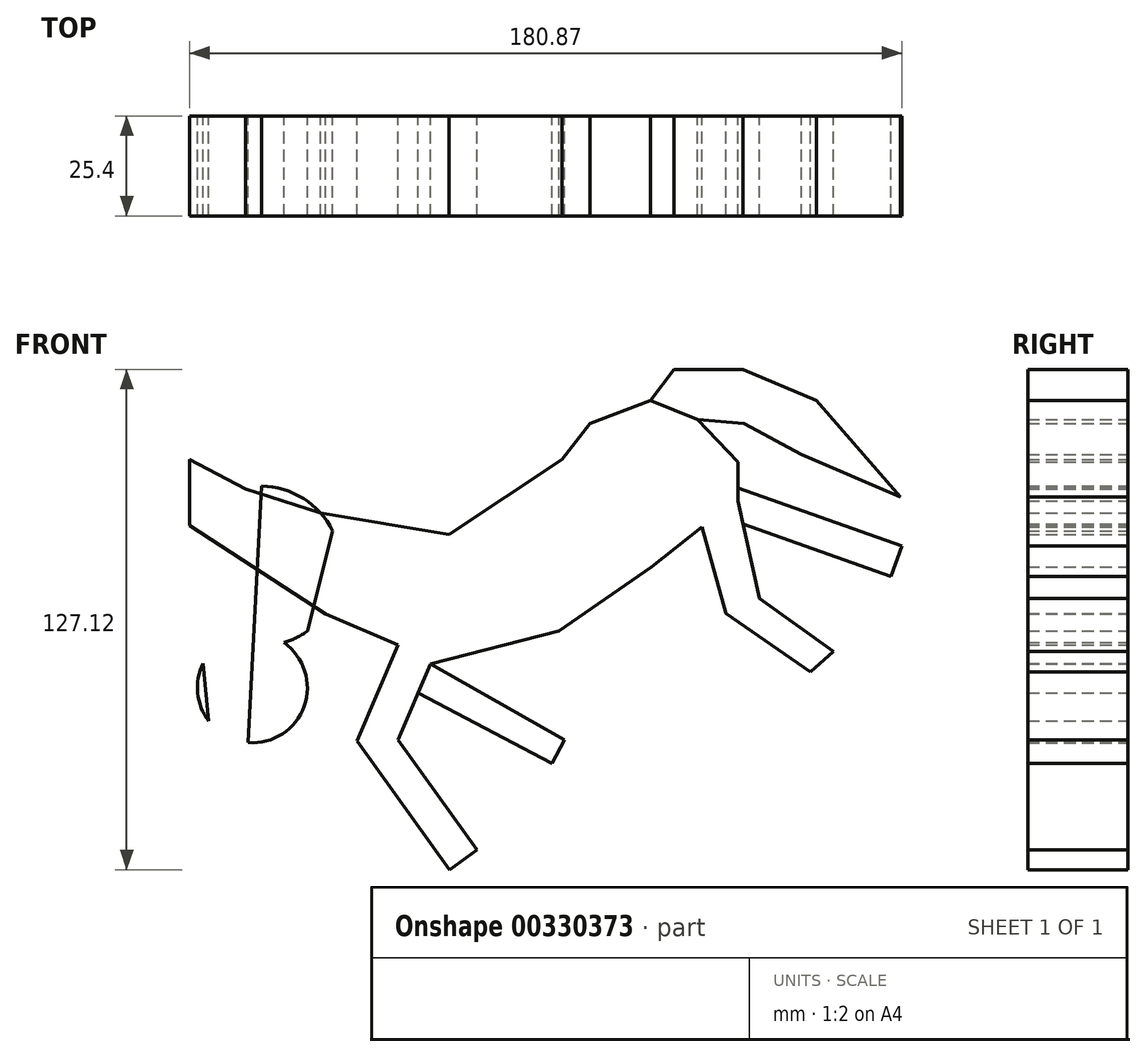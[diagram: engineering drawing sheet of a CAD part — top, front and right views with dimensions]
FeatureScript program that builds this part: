
annotation { "Feature Type Name" : "Feature", "Feature Type Description" : "" }
export const myFeature = defineFeature(function(context is Context, id is Id, definition is map)
    precondition{}
    {
        {
            var Q0;
            Q0=qCreatedBy(makeId("Front.planeOp"),FACE);
            var sketch = newSketch(context, id + "F0", { "sketchPlane" : qUnion([Q0])});
            skLineSegment(sketch, "E0.bottom", {"start": v(-85.46, 39.7) * mm, "end": v(65.16, 39.7) * mm});
            skLineSegment(sketch, "E0.top", {"start": v(-85.46, -39.7) * mm, "end": v(65.16, -39.7) * mm});
            skLineSegment(sketch, "E0.left", {"start": v(-85.46, 39.7) * mm, "end": v(-85.46, -39.7) * mm});
            skLineSegment(sketch, "E0.right", {"start": v(65.16, 39.7) * mm, "end": v(65.16, -39.7) * mm});
            skPoint(sketch, "E0.middle", {"position": v(-10.15, 0) * mm});
            skLineSegment(sketch, "E1.bottom", {"start": v(123.33, 72.62) * mm, "end": v(31.34, 72.62) * mm});
            skLineSegment(sketch, "E1.top", {"start": v(123.33, 122.22) * mm, "end": v(31.34, 122.22) * mm});
            skLineSegment(sketch, "E1.left", {"start": v(123.33, 72.62) * mm, "end": v(123.33, 122.22) * mm});
            skLineSegment(sketch, "E1.right", {"start": v(31.34, 72.62) * mm, "end": v(31.34, 122.22) * mm});
            skPoint(sketch, "E1.middle", {"position": v(77.33, 97.42) * mm});
            skLineSegment(sketch, "E2", {"start": v(68.31, 39.7) * mm, "end": v(77.33, 97.42) * mm});
            skLineSegment(sketch, "E3", {"start": v(77.33, 97.42) * mm, "end": v(-10.15, 90.2) * mm});
            skLineSegment(sketch, "E4", {"start": v(-10.15, 90.2) * mm, "end": v(-85.46, 39.7) * mm});
            skSolve(sketch);
        }
        {
            var Q0;
            Q0=makeQuery(id+"F0.imprint","IMPRINT",FACE,{"disambiguationData":[TD([[makeQuery(id+"F0.imprint","IMPRINT",EDGE,{"derivedFrom":sQuery(id+"F0.wireOp",EDGE,"E0.bottom")}),-1.0]])]});
            var Q1;
            {var subQ1=sQuery(id+"F0.wireOp",EDGE,"E1.top");Q1=makeQuery(id+"F0.imprint","IMPRINT",FACE,{"disambiguationData":[TD([[makeQuery(id+"F0.imprint","IMPRINT",EDGE,{"derivedFrom":subQ1}),1.0]])]});}
            var Q2;
            {var subQ0=sQuery(id+"F0.wireOp",EDGE,"E1.right");var subQ1=sQuery(id+"F0.wireOp",EDGE,"E1.bottom");var subQ2=makeQuery(id+"F0.imprint","INTERSECT",VERTEX,{"derivedFrom":[subQ1,subQ0]});Q2=makeQuery(id+"F0.imprint","IMPRINT",FACE,{"disambiguationData":[TD([[makeQuery(id+"F0.imprint","IMPRINT",EDGE,{"disambiguationData":[TD([[subQ2,1.0]])],"derivedFrom":subQ1}),-1.0]])]});}
            extrude(context, id + "F1", {"entities" : qUnion([Q0, Q1, Q2]), "endBound" : BoundingType.SYMMETRIC, "depth" : 127 * mm});
        }
        {
            var Q0;
            Q0=makeQuery(id+"F1.opExtrude","CAP_EDGE",EDGE,{"disambiguationData":[OSD([sQuery(id+"F0.wireOp",EDGE,"E0.top")])],"isStart":true});
            var Q1;
            Q1=makeQuery(id+"F1.opExtrude","CAP_EDGE",EDGE,{"disambiguationData":[OSD([sQuery(id+"F0.wireOp",EDGE,"E0.top")])],"isStart":false});
            fillet(context, id + "F2", {"entities" : qUnion([Q0, Q1]), "radius" : 101.6 * mm, "tangentPropagation" : true, "allowEdgeOverflow" : false});
        }
        {
            var Q0;
            {var subQ0=sQuery(id+"F0.wireOp",EDGE,"E0.top");Q0=makeQuery(id+"F2.opFillet","BLEND_EDGE",EDGE,{"blendedFrom":[makeQuery(id+"F1.opExtrude","CAP_EDGE",EDGE,{"disambiguationData":[OSD([subQ0])],"isStart":true}),makeQuery(id+"F1.opExtrude","CAP_EDGE",EDGE,{"disambiguationData":[OSD([subQ0])],"isStart":false})],"blendedInto":[]});}
            fillet(context, id + "F3", {"entities" : qUnion([Q0]), "radius" : 63.5 * mm, "tangentPropagation" : true, "allowEdgeOverflow" : false});
        }
        {
            var Q0;
            Q0=makeQuery(id+"F1.opExtrude","SWEPT_BODY",BODY,{"disambiguationData":[OSD([sQuery(id+"F0.wireOp",EDGE,"E0.bottom"),sQuery(id+"F0.wireOp",EDGE,"E0.top"),sQuery(id+"F0.wireOp",EDGE,"E0.left"),sQuery(id+"F0.wireOp",EDGE,"E0.right")])]});
            deleteBodies(context, id + "F4", {"entities" : qUnion([Q0])});
        }
        {
            var Q0;
            Q0=makeQuery(id+"F1.opExtrude","SWEPT_BODY",BODY,{"disambiguationData":[OSD([sQuery(id+"F0.wireOp",EDGE,"E1.bottom"),sQuery(id+"F0.wireOp",EDGE,"E1.top"),sQuery(id+"F0.wireOp",EDGE,"E1.left"),sQuery(id+"F0.wireOp",EDGE,"E1.right")])]});
            deleteBodies(context, id + "F5", {"entities" : qUnion([Q0])});
        }
        {
            var Q0;
            Q0=qCreatedBy(makeId("Front.planeOp"),FACE);
            var sketch = newSketch(context, id + "F6", { "sketchPlane" : qUnion([Q0])});
            skCircle(sketch, "E5", {"center": v(-36.98, 21.6) * mm, "radius": 13.97 * mm});
            skCircle(sketch, "E6", {"center": v(-34.9, 52.5) * mm, "radius": 20.32 * mm});
            skLineSegment(sketch, "E7", {"start": v(-36.6, 35.56) * mm, "end": v(-34.68, 72.82) * mm});
            skLineSegment(sketch, "E8", {"start": v(-34.68, 72.82) * mm, "end": v(-38.06, 7.67) * mm});
            skLineSegment(sketch, "E9", {"start": v(-49.5, 27.78) * mm, "end": v(-52.82, 62.05) * mm});
            skLineSegment(sketch, "E10", {"start": v(-52.82, 62.05) * mm, "end": v(-48.09, 13.13) * mm});
            skLineSegment(sketch, "E11", {"start": v(-24.86, 28.53) * mm, "end": v(-16.65, 61.45) * mm});
            skLineSegment(sketch, "E12", {"start": v(-16.65, 61.45) * mm, "end": v(-29.53, 9.79) * mm});
            skSolve(sketch);
        }
        {
            var Q0;
            {var subQ1=sQuery(id+"F6.wireOp",EDGE,"E6");var subQ3=sQuery(id+"F6.wireOp",EDGE,"E5");var subQ4=makeQuery(id+"F6.imprint","INTERSECT",VERTEX,{"disambiguationData":[OD(0.0)],"derivedFrom":[subQ3,subQ1]});Q0=makeQuery(id+"F6.imprint","IMPRINT",FACE,{"disambiguationData":[TD([[makeQuery(id+"F6.imprint","IMPRINT",EDGE,{"disambiguationData":[TD([[subQ4,-1.0]])],"derivedFrom":subQ3}),-1.0]])]});}
            var Q1;
            {var subQ0=sQuery(id+"F6.wireOp",EDGE,"E8");var subQ3=sQuery(id+"F6.wireOp",EDGE,"E5");var subQ4=makeQuery(id+"F6.imprint","INTERSECT",VERTEX,{"disambiguationData":[OD(1.0)],"derivedFrom":[subQ3,subQ0]});Q1=makeQuery(id+"F6.imprint","IMPRINT",FACE,{"disambiguationData":[TD([[makeQuery(id+"F6.imprint","IMPRINT",EDGE,{"disambiguationData":[TD([[subQ4,-1.0]])],"derivedFrom":subQ3}),-1.0]])]});}
            var Q2;
            {var subQ1=sQuery(id+"F6.wireOp",EDGE,"E5");var subQ6=sQuery(id+"F6.wireOp",EDGE,"E10");var subQ8=makeQuery(id+"F6.imprint","INTERSECT",VERTEX,{"disambiguationData":[OD(1.0)],"derivedFrom":[subQ1,subQ6]});Q2=makeQuery(id+"F6.imprint","IMPRINT",FACE,{"disambiguationData":[TD([[makeQuery(id+"F6.imprint","IMPRINT",EDGE,{"disambiguationData":[TD([[subQ8,1.0]])],"derivedFrom":subQ1}),1.0]])]});}
            var Q3;
            {var subQ1=sQuery(id+"F6.wireOp",EDGE,"E5");var subQ6=sQuery(id+"F6.wireOp",EDGE,"E12");var subQ8=makeQuery(id+"F6.imprint","INTERSECT",VERTEX,{"disambiguationData":[OD(1.0)],"derivedFrom":[subQ1,subQ6]});Q3=makeQuery(id+"F6.imprint","IMPRINT",FACE,{"disambiguationData":[TD([[makeQuery(id+"F6.imprint","IMPRINT",EDGE,{"disambiguationData":[TD([[subQ8,-1.0]])],"derivedFrom":subQ1}),1.0]])]});}
            var Q4;
            {var subQ0=sQuery(id+"F6.wireOp",EDGE,"E12");var subQ1=sQuery(id+"F6.wireOp",EDGE,"E6");var subQ2=makeQuery(id+"F6.imprint","INTERSECT",VERTEX,{"disambiguationData":[OD(0.0)],"derivedFrom":[subQ1,subQ0]});Q4=makeQuery(id+"F6.imprint","IMPRINT",FACE,{"disambiguationData":[TD([[makeQuery(id+"F6.imprint","IMPRINT",EDGE,{"disambiguationData":[TD([[subQ2,1.0]])],"derivedFrom":subQ1}),1.0]])]});}
            var Q5;
            {var subQ0=sQuery(id+"F6.wireOp",EDGE,"E6");var subQ1=sQuery(id+"F6.wireOp",EDGE,"E5");var subQ2=makeQuery(id+"F6.imprint","INTERSECT",VERTEX,{"disambiguationData":[OD(0.0)],"derivedFrom":[subQ1,subQ0]});Q5=makeQuery(id+"F6.imprint","IMPRINT",FACE,{"disambiguationData":[TD([[makeQuery(id+"F6.imprint","IMPRINT",EDGE,{"disambiguationData":[TD([[subQ2,-1.0]])],"derivedFrom":subQ1}),1.0]])]});}
            var Q6;
            {var subQ0=sQuery(id+"F6.wireOp",EDGE,"E10");var subQ1=sQuery(id+"F6.wireOp",EDGE,"E6");var subQ2=makeQuery(id+"F6.imprint","INTERSECT",VERTEX,{"disambiguationData":[OD(0.0)],"derivedFrom":[subQ1,subQ0]});Q6=makeQuery(id+"F6.imprint","IMPRINT",FACE,{"disambiguationData":[TD([[makeQuery(id+"F6.imprint","IMPRINT",EDGE,{"disambiguationData":[TD([[subQ2,-1.0]])],"derivedFrom":subQ1}),1.0]])]});}
            var Q7;
            {var subQ0=sQuery(id+"F6.wireOp",EDGE,"E8");var subQ1=sQuery(id+"F6.wireOp",EDGE,"E5");var subQ2=makeQuery(id+"F6.imprint","INTERSECT",VERTEX,{"disambiguationData":[OD(1.0)],"derivedFrom":[subQ1,subQ0]});Q7=makeQuery(id+"F6.imprint","IMPRINT",FACE,{"disambiguationData":[TD([[makeQuery(id+"F6.imprint","IMPRINT",EDGE,{"disambiguationData":[TD([[subQ2,-1.0]])],"derivedFrom":subQ1}),1.0]])]});}
            var Q8;
            {var subQ0=sQuery(id+"F6.wireOp",EDGE,"E10");var subQ1=sQuery(id+"F6.wireOp",EDGE,"E5");var subQ2=makeQuery(id+"F6.imprint","INTERSECT",VERTEX,{"disambiguationData":[OD(1.0)],"derivedFrom":[subQ1,subQ0]});Q8=makeQuery(id+"F6.imprint","IMPRINT",FACE,{"disambiguationData":[TD([[makeQuery(id+"F6.imprint","IMPRINT",EDGE,{"disambiguationData":[TD([[subQ2,1.0]])],"derivedFrom":subQ1}),-1.0]])]});}
            var Q9;
            {var subQ0=sQuery(id+"F6.wireOp",EDGE,"E12");var subQ1=sQuery(id+"F6.wireOp",EDGE,"E5");var subQ2=makeQuery(id+"F6.imprint","INTERSECT",VERTEX,{"disambiguationData":[OD(1.0)],"derivedFrom":[subQ1,subQ0]});Q9=makeQuery(id+"F6.imprint","IMPRINT",FACE,{"disambiguationData":[TD([[makeQuery(id+"F6.imprint","IMPRINT",EDGE,{"disambiguationData":[TD([[subQ2,-1.0]])],"derivedFrom":subQ1}),-1.0]])]});}
            var Q10;
            {var subQ0=sQuery(id+"F6.wireOp",EDGE,"E12");var subQ1=sQuery(id+"F6.wireOp",EDGE,"E5");var subQ2=makeQuery(id+"F6.imprint","INTERSECT",VERTEX,{"disambiguationData":[OD(0.0)],"derivedFrom":[subQ1,subQ0]});Q10=makeQuery(id+"F6.imprint","IMPRINT",FACE,{"disambiguationData":[TD([[makeQuery(id+"F6.imprint","IMPRINT",EDGE,{"disambiguationData":[TD([[subQ2,-1.0]])],"derivedFrom":subQ1}),1.0]])]});}
            var Q11;
            {var subQ0=sQuery(id+"F6.wireOp",EDGE,"E10");var subQ1=sQuery(id+"F6.wireOp",EDGE,"E5");var subQ2=makeQuery(id+"F6.imprint","INTERSECT",VERTEX,{"disambiguationData":[OD(0.0)],"derivedFrom":[subQ1,subQ0]});Q11=makeQuery(id+"F6.imprint","IMPRINT",FACE,{"disambiguationData":[TD([[makeQuery(id+"F6.imprint","IMPRINT",EDGE,{"disambiguationData":[TD([[subQ2,1.0]])],"derivedFrom":subQ1}),1.0]])]});}
            extrude(context, id + "F7", {"entities" : qUnion([Q0, Q1, Q2, Q3, Q4, Q5, Q6, Q7, Q8, Q9, Q10, Q11]), "endBound" : BoundingType.SYMMETRIC, "depth" : 25.4 * mm});
        }
        {
            var Q0;
            Q0=qCreatedBy(makeId("Front.planeOp"),FACE);
            var sketch = newSketch(context, id + "F8", { "sketchPlane" : qUnion([Q0])});
            skLineSegment(sketch, "E13", {"start": v(-52.9, 62.8) * mm, "end": v(-52.9, 79.65) * mm});
            skLineSegment(sketch, "E14", {"start": v(-52.9, 79.65) * mm, "end": v(-38.71, 72.05) * mm});
            skLineSegment(sketch, "E15", {"start": v(-19.72, 65.95) * mm, "end": v(12.96, 60.57) * mm});
            skLineSegment(sketch, "E16", {"start": v(-18.35, 40.3) * mm, "end": v(0, 32.44) * mm});
            skLineSegment(sketch, "E17", {"start": v(0, 32.44) * mm, "end": v(-10.43, 8.08) * mm});
            skLineSegment(sketch, "E18", {"start": v(-10.43, 8.08) * mm, "end": v(13.03, -24.6) * mm});
            skLineSegment(sketch, "E19", {"start": v(13.03, -24.6) * mm, "end": v(20.06, -19.56) * mm});
            skLineSegment(sketch, "E20", {"start": v(20.06, -19.56) * mm, "end": v(0, 8.39) * mm});
            skLineSegment(sketch, "E21", {"start": v(0, 8.39) * mm, "end": v(8.25, 27.65) * mm});
            skLineSegment(sketch, "E22", {"start": v(8.25, 27.65) * mm, "end": v(40.95, 36.03) * mm});
            skLineSegment(sketch, "E23", {"start": v(40.95, 36.03) * mm, "end": v(64.46, 52.27) * mm});
            skLineSegment(sketch, "E24", {"start": v(12.96, 60.57) * mm, "end": v(41.68, 79.6) * mm});
            skLineSegment(sketch, "E25", {"start": v(41.68, 79.6) * mm, "end": v(48.84, 88.72) * mm});
            skLineSegment(sketch, "E26", {"start": v(48.84, 88.72) * mm, "end": v(64.16, 94.53) * mm});
            skLineSegment(sketch, "E27", {"start": v(64.16, 94.53) * mm, "end": v(76.02, 89.75) * mm});
            skLineSegment(sketch, "E28", {"start": v(76.02, 89.75) * mm, "end": v(86.41, 79) * mm});
            skLineSegment(sketch, "E29", {"start": v(86.41, 79) * mm, "end": v(86.41, 69.1) * mm});
            skLineSegment(sketch, "E30", {"start": v(86.41, 69.1) * mm, "end": v(91.8, 44.26) * mm});
            skLineSegment(sketch, "E31", {"start": v(91.8, 44.26) * mm, "end": v(110.6, 30.89) * mm});
            skLineSegment(sketch, "E32", {"start": v(110.6, 30.89) * mm, "end": v(104.78, 25.6) * mm});
            skLineSegment(sketch, "E33", {"start": v(104.78, 25.6) * mm, "end": v(83.3, 40.46) * mm});
            skLineSegment(sketch, "E34", {"start": v(83.3, 40.46) * mm, "end": v(77.18, 62.41) * mm});
            skLineSegment(sketch, "E35", {"start": v(77.18, 62.41) * mm, "end": v(64.46, 52.27) * mm});
            skLineSegment(sketch, "E36", {"start": v(64.16, 94.53) * mm, "end": v(70.17, 102.5) * mm});
            skLineSegment(sketch, "E37", {"start": v(70.17, 102.5) * mm, "end": v(87.63, 102.5) * mm});
            skLineSegment(sketch, "E38", {"start": v(87.63, 102.5) * mm, "end": v(106.26, 94.53) * mm});
            skLineSegment(sketch, "E39", {"start": v(106.26, 94.53) * mm, "end": v(127.67, 70.12) * mm});
            skLineSegment(sketch, "E40", {"start": v(127.67, 70.12) * mm, "end": v(102.5, 80.9) * mm});
            skLineSegment(sketch, "E41", {"start": v(102.5, 80.9) * mm, "end": v(87.91, 88.72) * mm});
            skLineSegment(sketch, "E42", {"start": v(87.91, 88.72) * mm, "end": v(76.02, 89.75) * mm});
            skLineSegment(sketch, "E43", {"start": v(5.1, 20.32) * mm, "end": v(39.16, 2.33) * mm});
            skLineSegment(sketch, "E44", {"start": v(39.16, 2.33) * mm, "end": v(42.33, 8.3) * mm});
            skLineSegment(sketch, "E45", {"start": v(42.33, 8.3) * mm, "end": v(8.25, 27.65) * mm});
            skLineSegment(sketch, "E46", {"start": v(86.41, 72.38) * mm, "end": v(127.97, 57.63) * mm});
            skLineSegment(sketch, "E47", {"start": v(127.97, 57.63) * mm, "end": v(125.24, 49.93) * mm});
            skLineSegment(sketch, "E48", {"start": v(125.24, 49.93) * mm, "end": v(87.68, 63.27) * mm});
            skLineSegment(sketch, "E49", {"start": v(-38.71, 72.05) * mm, "end": v(-19.72, 65.95) * mm});
            skLineSegment(sketch, "E50", {"start": v(-52.9, 62.8) * mm, "end": v(-18.35, 40.3) * mm});
            skSolve(sketch);
        }
        {
            var Q0;
            Q0=makeQuery(id+"F8.imprint","IMPRINT",FACE,{"disambiguationData":[TD([[makeQuery(id+"F8.imprint","IMPRINT",EDGE,{"derivedFrom":sQuery(id+"F8.wireOp",EDGE,"E27")}),1.0]])]});
            var Q1;
            {var subQ0=sQuery(id+"F8.wireOp",EDGE,"E46");Q1=makeQuery(id+"F8.imprint","IMPRINT",FACE,{"disambiguationData":[TD([[makeQuery(id+"F8.imprint","IMPRINT",EDGE,{"derivedFrom":subQ0}),-1.0]])]});}
            var Q2;
            {var subQ2=sQuery(id+"F8.wireOp",EDGE,"E43");Q2=makeQuery(id+"F8.imprint","IMPRINT",FACE,{"disambiguationData":[TD([[makeQuery(id+"F8.imprint","IMPRINT",EDGE,{"derivedFrom":subQ2}),1.0]])]});}
            extrude(context, id + "F9", {"entities" : qUnion([Q0, Q1, Q2]), "endBound" : BoundingType.SYMMETRIC, "depth" : 25.4 * mm});
        }
        {
            var Q0;
            Q0=makeQuery(id+"F8.imprint","IMPRINT",FACE,{"disambiguationData":[TD([[makeQuery(id+"F8.imprint","IMPRINT",EDGE,{"derivedFrom":sQuery(id+"F8.wireOp",EDGE,"E13")}),-1.0]])]});
            extrude(context, id + "F10", {"entities" : qUnion([Q0]), "endBound" : BoundingType.SYMMETRIC, "depth" : 25.4 * mm});
        }
    });
